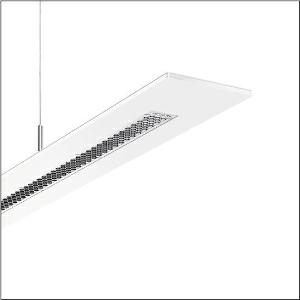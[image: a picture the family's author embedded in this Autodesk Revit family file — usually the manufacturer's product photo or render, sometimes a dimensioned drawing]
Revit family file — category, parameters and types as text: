
# Revit family: arktika_r__21_5mb2512l30840_559e
name_source: partatom
category: Lighting Fixtures
units: mm (PartAtom-declared; Revit-internal decimal feet)

## family parameters
Cut with Voids When Loaded = No
Host = Face
Light Source = No
Part Type = Normal
Room Calculation Point = No
Round Connector Dimension = Use Diameter
Shared = No

## types (1)
- Arktika® 21 (1 x LED 4000K / CRI = 80 (unbekannt), 4000 lm, 4000K)
    Apparent Load = 31 VA
    CIE Flux Codes = 81 100 100 79 100
    Color Rendering = 80
    Color Temperature = 4000K
    Default Elevation = 1800 mm
    Description = Arktika® 21, office luminaire, primary anti-glare with honeycomb louvre, of plastic, aluminium vaporised, highly specular, light emission: direct/indirect distribution, primary light characteristic: symmetric, installation type: suspended mounting, LED, rated luminous flux: 4.000lm, luminous efficacy: 130lm/W, light colour: 840, colour temperature: 4000K, control gear: ECG, with terminal, 3-pole, mains connection: 220..240V, AC, 50/60Hz, rated input power: 31W, housing, of aluminium, powder-coated, traffic white (RAL 9016), 1-length, length: 1.250mm, width: 120mm, height: 8mm, protection rating (complete): IP20, insulation class (complete): insulation class II (safety insulation), certification: CE, packaging unit: 1 piece
    Height = 8 mm  [stored 0.0262467 ft]
    Lamp = 1 x LED 4000K / CRI >= 80 (unbekannt)
    Lamp Light Flux = 4000 lm
    Lamp count = 1
    Length = 1250 mm
    Luminous efficacy = 130 lm/W
    Manufacturer = Siteco
    ModVariant = No
    Model = 5MB2512L30840
    Mounting Place = Ceiling
    Mounting Type = Pendant
    Number of Poles = 1
    OnlyDefault = Yes
    Power Factor = 1
    Product Name = Arktika® 21
    Product group = office luminaire | ceiling pendant
    ProductGroupID = 902
    Protection Class = Protection class II
    Protection Degree = IP 20
    RLX_Detail_Level = 1
    RLX_Emergency_Light_Flux = 0 lm
    RLX_Emergency_Type = 0
    RLX_Emergency_Type_DB = No
    RlxData = <blob elided: 36053 chars, md5=f32ba11c>
    Socket = socket
    Standby Power = 0 W
    System Light Flux = 4000 lm
    System Power = 31 W
    Type Comments = Product without accessories
    Type Image = l_1006128.jpg
    URL = http://relux.com
    VarID = ---
    Voltage = 0 V
    Weight = 0.00 kg
    Width = 120 mm

note: [stored X ft] marks values corroborated as IEEE doubles in the binary element streams (Revit-internal decimal feet)

## geometry (parser evidence)
native form markers: Blend x4, Sweep x12
no freeform markers — native parametric forms only
